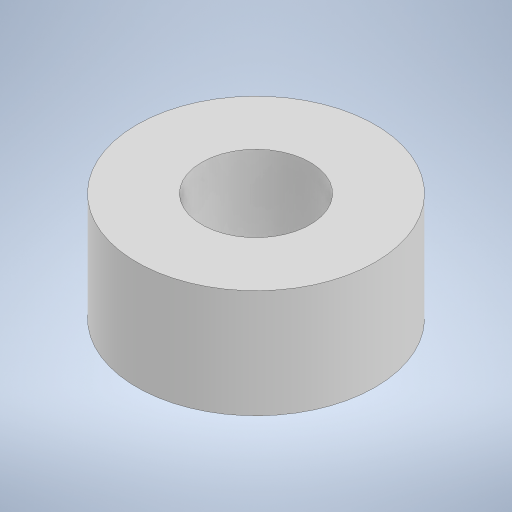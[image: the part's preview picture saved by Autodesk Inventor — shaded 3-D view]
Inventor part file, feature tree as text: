
AUTODESK INVENTOR PART (.ipt)
format: ipt  version: 2024 (Build 280153000, 153)  size: 199,168 bytes
history: native  units: in
note: dims shown in document units (in); Inventor stores cm internally (conversion verified against a paired STEP export)
features: extrude x1, sketch x1
ambient origin geometry x8: Origin, YZ Plane, XZ Plane, XY Plane, X Axis, Y Axis, Z Axis, Center Point
bodies: Solid1 (feature_tree)
feature tree (2):
  extrude  "Extrusion1"  Depth=0.1969in
  sketch  "Sketch1"  dims[d0=0.1969in d1=0.4331in d2=0.1969in d3=0.0in]
